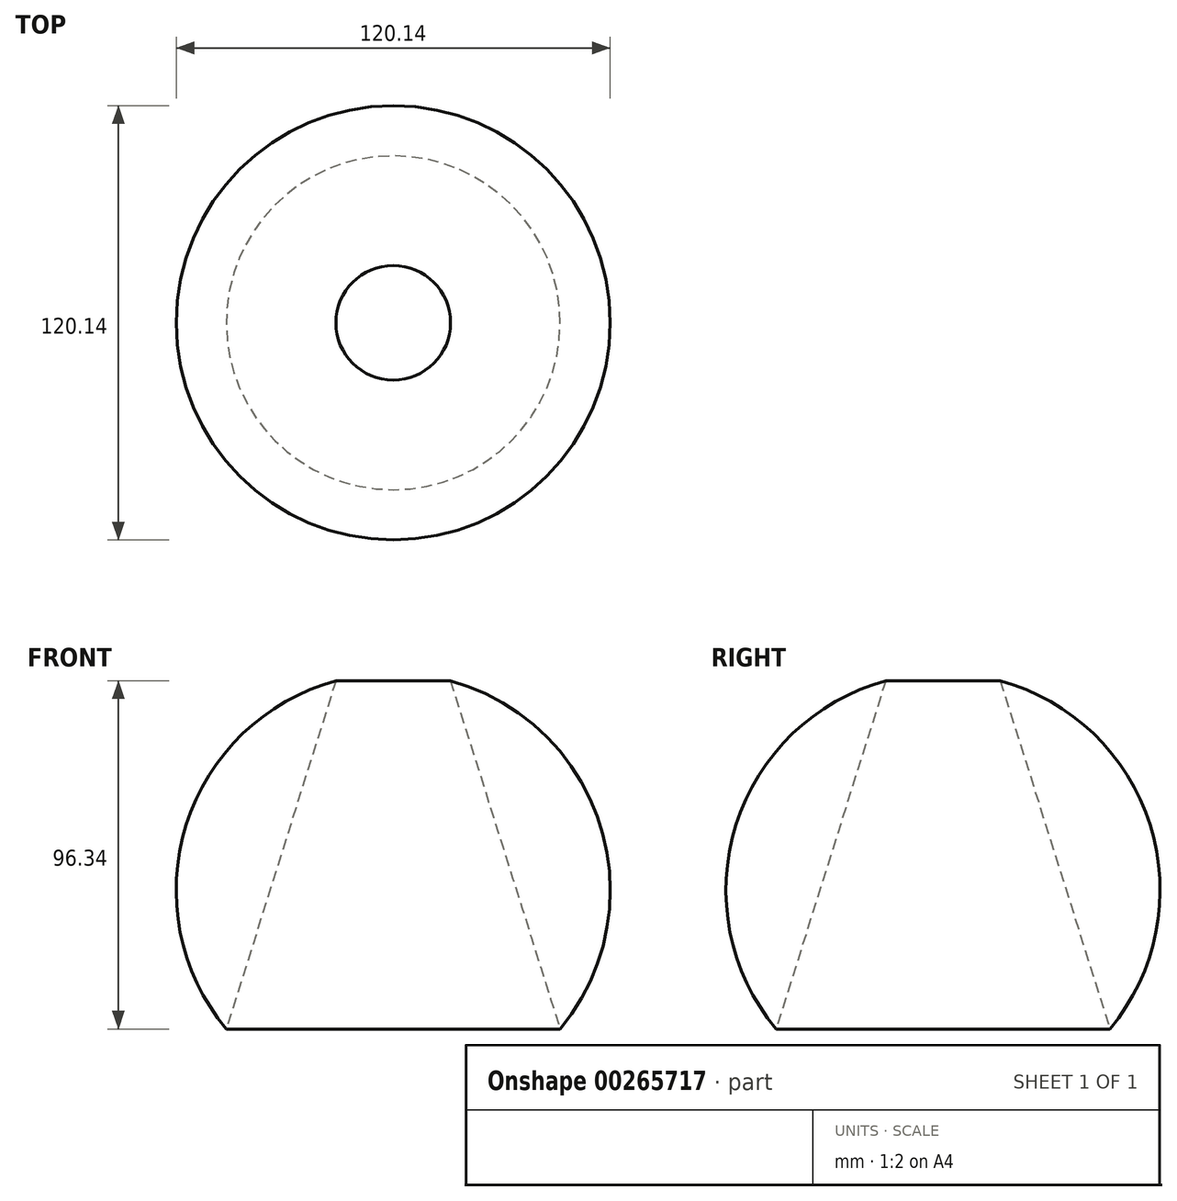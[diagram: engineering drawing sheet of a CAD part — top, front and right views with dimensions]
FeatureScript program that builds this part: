
annotation { "Feature Type Name" : "Feature", "Feature Type Description" : "" }
export const myFeature = defineFeature(function(context is Context, id is Id, definition is map)
    precondition{}
    {
        {
            var Q0;
            Q0=qCreatedBy(makeId("Front.planeOp"),FACE);
            var sketch = newSketch(context, id + "F0", { "sketchPlane" : qUnion([Q0])});
            skLineSegment(sketch, "E0", {"start": v(0, 60.07) * mm, "end": v(0, -60.07) * mm});
            skArc(sketch, "E1", {"start": v(0, -60.07) * mm, "mid": v(60.07, 0) * mm, "end": v(0, 60.07) * mm});
            skLineSegment(sketch, "E2", {"start": v(15.86, 57.93) * mm, "end": v(46.19, -38.4) * mm});
            skSolve(sketch);
        }
        {
            var Q0;
            {var subQ0=sQuery(id+"F0.wireOp",EDGE,"E2");Q0=makeQuery(id+"F0.imprint","IMPRINT",FACE,{"disambiguationData":[TD([[makeQuery(id+"F0.imprint","IMPRINT",EDGE,{"derivedFrom":subQ0}),1.0]])]});}
            var Q1;
            Q1=sQuery(id+"F0.wireOp",EDGE,"E0");
            revolve(context, id + "F1", {"entities" : qUnion([Q0]), "axis" : qUnion([Q1]), "revolveType" : RevolveType.FULL});
        }
    });
